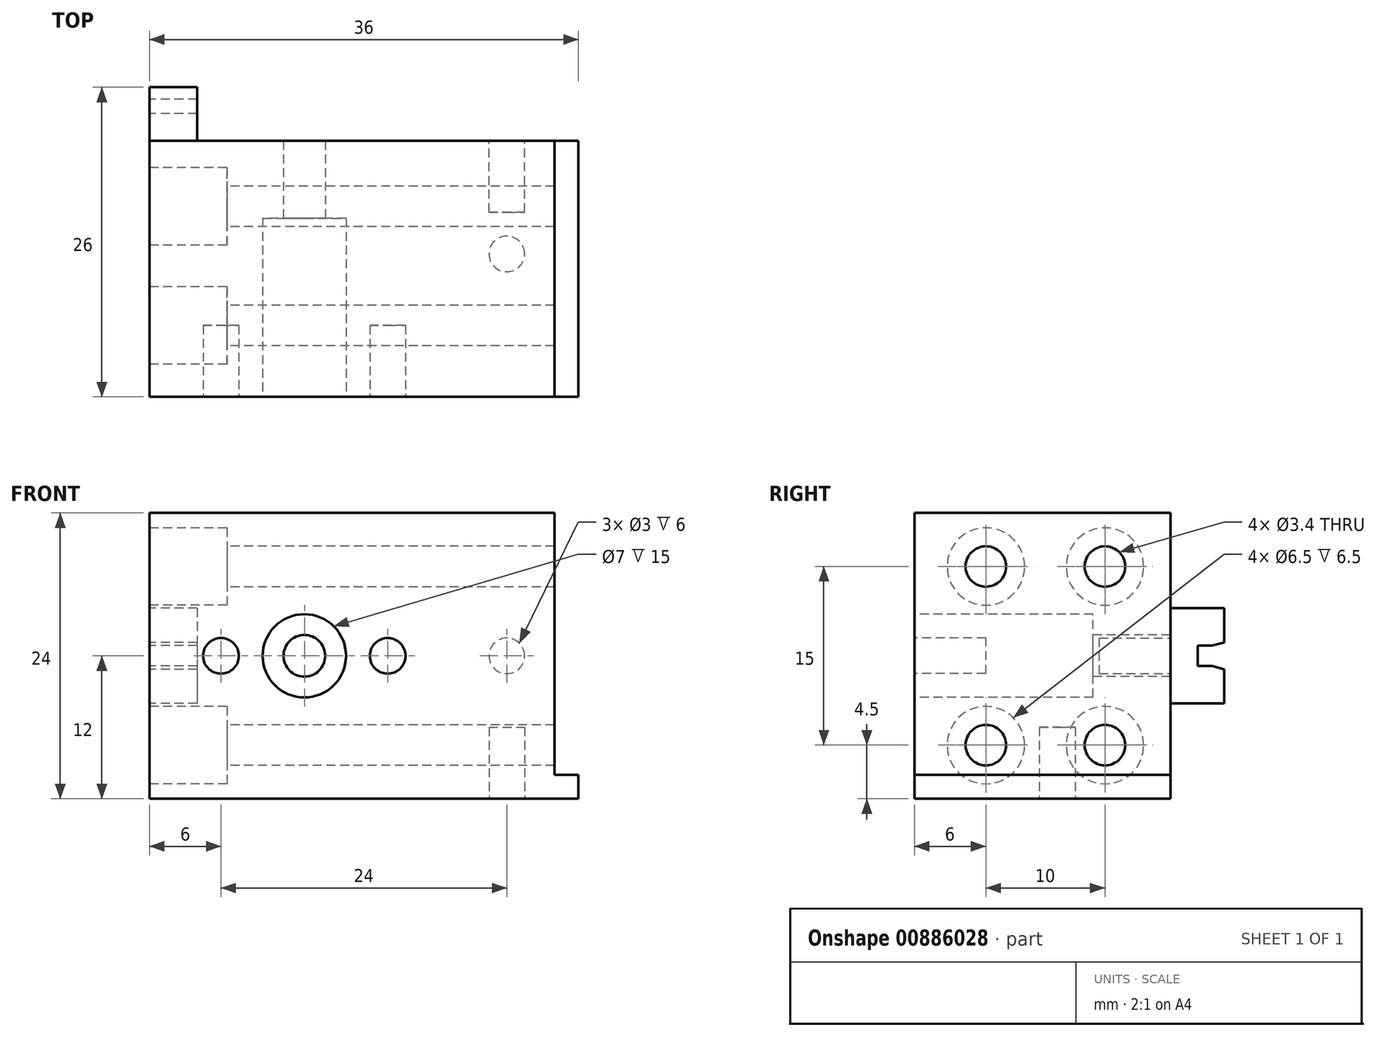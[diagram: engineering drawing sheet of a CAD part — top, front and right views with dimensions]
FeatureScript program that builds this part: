
annotation { "Feature Type Name" : "Feature", "Feature Type Description" : "" }
export const myFeature = defineFeature(function(context is Context, id is Id, definition is map)
    precondition{}
    {
        {
            var Q0;
            Q0=qCreatedBy(makeId("Front.planeOp"),FACE);
            var sketch = newSketch(context, id + "F0", { "sketchPlane" : qUnion([Q0])});
            skLineSegment(sketch, "E0.bottom", {"start": v(-18, 12) * mm, "end": v(18, 12) * mm});
            skLineSegment(sketch, "E0.top", {"start": v(-18, -12) * mm, "end": v(18, -12) * mm});
            skLineSegment(sketch, "E0.left", {"start": v(-18, 12) * mm, "end": v(-18, -12) * mm});
            skLineSegment(sketch, "E0.right", {"start": v(18, 12) * mm, "end": v(18, -12) * mm});
            skPoint(sketch, "E0.middle", {"position": v(0, 0) * mm});
            skSolve(sketch);
        }
        {
            var Q0;
            Q0 = qSketchRegion(id + "F0", true);
            extrude(context, id + "F1", {"entities" : qUnion([Q0]), "depth" : 21.5 * mm, "offsetDistance" : 25 * mm});
        }
        {
            var Q0;
            Q0=makeQuery(id+"F1.opExtrude","SWEPT_FACE",FACE,{"disambiguationData":[OSD([sQuery(id+"F0.wireOp",EDGE,"E0.left")])]});
            var sketch = newSketch(context, id + "F2", { "sketchPlane" : qUnion([Q0])});
            skCircle(sketch, "E1", {"center": v(15.5, 7.5) * mm, "radius": 1.7 * mm});
            skCircle(sketch, "E2", {"center": v(5.5, -7.5) * mm, "radius": 1.7 * mm});
            skCircle(sketch, "E3", {"center": v(5.5, 7.5) * mm, "radius": 1.7 * mm});
            skCircle(sketch, "E4", {"center": v(15.5, -7.5) * mm, "radius": 1.7 * mm});
            skSolve(sketch);
        }
        {
            var Q0;
            Q0 = qSketchRegion(id + "F2", true);
            extrude(context, id + "F3", {"entities" : qUnion([Q0]), "operationType" : NewBodyOperationType.REMOVE, "endBound" : BoundingType.THROUGH_ALL, "oppositeDirection" : true, "depth" : 25 * mm, "offsetDistance" : 25 * mm});
        }
        {
            var Q0;
            Q0=makeQuery(id+"F1.opExtrude","SWEPT_FACE",FACE,{"disambiguationData":[OSD([sQuery(id+"F0.wireOp",EDGE,"E0.left")])]});
            var sketch = newSketch(context, id + "F4", { "sketchPlane" : qUnion([Q0])});
            skLineSegment(sketch, "E5.bottom", {"start": v(0, 4) * mm, "end": v(-4.5, 4) * mm});
            skLineSegment(sketch, "E5.top", {"start": v(0, -4) * mm, "end": v(-4.5, -4) * mm});
            skLineSegment(sketch, "E5.left", {"start": v(0, 4) * mm, "end": v(0, -4) * mm});
            skLineSegment(sketch, "E5.right", {"start": v(-4.5, 4) * mm, "end": v(-4.5, 1.13) * mm});
            skLineSegment(sketch, "E6.bottom", {"start": v(-3.5, 0.86) * mm, "end": v(-2.3, 0.86) * mm});
            skLineSegment(sketch, "E6.top", {"start": v(-3.5, -0.86) * mm, "end": v(-2.3, -0.86) * mm});
            skLineSegment(sketch, "E6.right", {"start": v(-2.3, 0.86) * mm, "end": v(-2.3, -0.86) * mm});
            skLineSegment(sketch, "E7.trimOffspring", {"start": v(-4.5, -1.13) * mm, "end": v(-4.5, -4) * mm});
            skLineSegment(sketch, "E8", {"start": v(-3.5, -0.86) * mm, "end": v(-4.5, -1.13) * mm});
            skLineSegment(sketch, "E9.MirrorCS", {"start": v(-3.5, 0.86) * mm, "end": v(-4.5, 1.13) * mm});
            skSolve(sketch);
        }
        {
            var Q0;
            Q0 = qSketchRegion(id + "F4", true);
            extrude(context, id + "F5", {"entities" : qUnion([Q0]), "operationType" : NewBodyOperationType.ADD, "oppositeDirection" : true, "depth" : 4 * mm, "offsetDistance" : 25 * mm});
        }
        {
            var Q0;
            Q0=makeQuery(id+"F5.boolean.opBoolean","MERGE",FACE,{"derivedFrom":[makeQuery(id+"F1.opExtrude","SWEPT_FACE",FACE,{"disambiguationData":[OSD([sQuery(id+"F0.wireOp",EDGE,"E0.left")])]}),makeQuery(id+"F5.opExtrude","CAP_FACE",FACE,{"disambiguationData":[OSD([sQuery(id+"F4.wireOp",EDGE,"E5.bottom"),sQuery(id+"F4.wireOp",EDGE,"E5.top"),sQuery(id+"F4.wireOp",EDGE,"E5.left"),sQuery(id+"F4.wireOp",EDGE,"E5.right"),sQuery(id+"F4.wireOp",EDGE,"E6.bottom"),sQuery(id+"F4.wireOp",EDGE,"E6.top"),sQuery(id+"F4.wireOp",EDGE,"E6.right"),sQuery(id+"F4.wireOp",EDGE,"E7.trimOffspring"),sQuery(id+"F4.wireOp",EDGE,"E8"),sQuery(id+"F4.wireOp",EDGE,"E9.MirrorCS")])],"isStart":true})]});
            var sketch = newSketch(context, id + "F6", { "sketchPlane" : qUnion([Q0])});
            skCircle(sketch, "E10", {"center": v(15.5, 7.5) * mm, "radius": 3.25 * mm});
            skCircle(sketch, "E11", {"center": v(5.5, 7.5) * mm, "radius": 3.25 * mm});
            skCircle(sketch, "E12", {"center": v(5.5, -7.5) * mm, "radius": 3.25 * mm});
            skCircle(sketch, "E13", {"center": v(15.5, -7.5) * mm, "radius": 3.25 * mm});
            skSolve(sketch);
        }
        {
            var Q0;
            Q0 = qSketchRegion(id + "F6", true);
            extrude(context, id + "F7", {"entities" : qUnion([Q0]), "operationType" : NewBodyOperationType.REMOVE, "oppositeDirection" : true, "depth" : 6.5 * mm, "offsetDistance" : 25 * mm});
        }
        {
            var Q0;
            Q0=makeQuery(id+"F1.opExtrude","CAP_FACE",FACE,{"disambiguationData":[OSD([sQuery(id+"F0.wireOp",EDGE,"E0.bottom"),sQuery(id+"F0.wireOp",EDGE,"E0.top"),sQuery(id+"F0.wireOp",EDGE,"E0.left"),sQuery(id+"F0.wireOp",EDGE,"E0.right")])],"isStart":false});
            var sketch = newSketch(context, id + "F8", { "sketchPlane" : qUnion([Q0])});
            skCircle(sketch, "E14", {"center": v(-12, 0) * mm, "radius": 1.5 * mm});
            skPoint(sketch, "E14.centerSnap0", {"position": v(-18, 0) * mm});
            skCircle(sketch, "E15", {"center": v(2, 0) * mm, "radius": 1.5 * mm});
            skSolve(sketch);
        }
        {
            var Q0;
            Q0 = qSketchRegion(id + "F8", true);
            extrude(context, id + "F9", {"entities" : qUnion([Q0]), "operationType" : NewBodyOperationType.REMOVE, "oppositeDirection" : true, "depth" : 6 * mm, "offsetDistance" : 25 * mm});
        }
        {
            var Q0;
            Q0=makeQuery(id+"F1.opExtrude","CAP_FACE",FACE,{"disambiguationData":[OSD([sQuery(id+"F0.wireOp",EDGE,"E0.bottom"),sQuery(id+"F0.wireOp",EDGE,"E0.top"),sQuery(id+"F0.wireOp",EDGE,"E0.left"),sQuery(id+"F0.wireOp",EDGE,"E0.right")])],"isStart":false});
            var sketch = newSketch(context, id + "F10", { "sketchPlane" : qUnion([Q0])});
            skLineSegment(sketch, "E16.bottom", {"start": v(18, 12) * mm, "end": v(16, 12) * mm});
            skLineSegment(sketch, "E16.top", {"start": v(18, -10) * mm, "end": v(16, -10) * mm});
            skLineSegment(sketch, "E16.left", {"start": v(18, 12) * mm, "end": v(18, -10) * mm});
            skLineSegment(sketch, "E16.right", {"start": v(16, 12) * mm, "end": v(16, -10) * mm});
            skCircle(sketch, "E17", {"center": v(-5, 0) * mm, "radius": 1.75 * mm});
            skSolve(sketch);
        }
        {
            var Q0;
            Q0 = qSketchRegion(id + "F10", true);
            extrude(context, id + "F11", {"entities" : qUnion([Q0]), "operationType" : NewBodyOperationType.REMOVE, "endBound" : BoundingType.THROUGH_ALL, "oppositeDirection" : true, "depth" : 25 * mm, "offsetDistance" : 25 * mm});
        }
        {
            var Q0;
            Q0=makeQuery(id+"F1.opExtrude","CAP_FACE",FACE,{"disambiguationData":[OSD([sQuery(id+"F0.wireOp",EDGE,"E0.bottom"),sQuery(id+"F0.wireOp",EDGE,"E0.top"),sQuery(id+"F0.wireOp",EDGE,"E0.left"),sQuery(id+"F0.wireOp",EDGE,"E0.right")])],"isStart":false});
            var sketch = newSketch(context, id + "F12", { "sketchPlane" : qUnion([Q0])});
            skCircle(sketch, "E18", {"center": v(-5, 0) * mm, "radius": 3.5 * mm});
            skSolve(sketch);
        }
        {
            var Q0;
            Q0 = qSketchRegion(id + "F12", true);
            extrude(context, id + "F13", {"entities" : qUnion([Q0]), "operationType" : NewBodyOperationType.REMOVE, "oppositeDirection" : true, "depth" : 15 * mm, "offsetDistance" : 25 * mm});
        }
        {
            var Q0;
            Q0=makeQuery(id+"F1.opExtrude","SWEPT_FACE",FACE,{"disambiguationData":[OSD([sQuery(id+"F0.wireOp",EDGE,"E0.top")])]});
            var sketch = newSketch(context, id + "F14", { "sketchPlane" : qUnion([Q0])});
            skCircle(sketch, "E19", {"center": v(12, 9.5) * mm, "radius": 1.5 * mm});
            skSolve(sketch);
        }
        {
            var Q0;
            Q0 = qSketchRegion(id + "F14", true);
            extrude(context, id + "F15", {"entities" : qUnion([Q0]), "operationType" : NewBodyOperationType.REMOVE, "oppositeDirection" : true, "depth" : 6 * mm, "offsetDistance" : 25 * mm});
        }
        {
            var Q0;
            Q0=makeQuery(id+"F1.opExtrude","CAP_FACE",FACE,{"disambiguationData":[OSD([sQuery(id+"F0.wireOp",EDGE,"E0.bottom"),sQuery(id+"F0.wireOp",EDGE,"E0.top"),sQuery(id+"F0.wireOp",EDGE,"E0.left"),sQuery(id+"F0.wireOp",EDGE,"E0.right")])],"isStart":true});
            var sketch = newSketch(context, id + "F16", { "sketchPlane" : qUnion([Q0])});
            skCircle(sketch, "E20", {"center": v(-12, 0) * mm, "radius": 1.5 * mm});
            skSolve(sketch);
        }
        {
            var Q0;
            Q0 = qSketchRegion(id + "F16", true);
            extrude(context, id + "F17", {"entities" : qUnion([Q0]), "operationType" : NewBodyOperationType.REMOVE, "flatOperationType" : FlatOperationType.REMOVE, "oppositeDirection" : true, "depth" : 6 * mm, "offsetDistance" : 25 * mm, "domain" : OperationDomain.MODEL});
        }
    });
